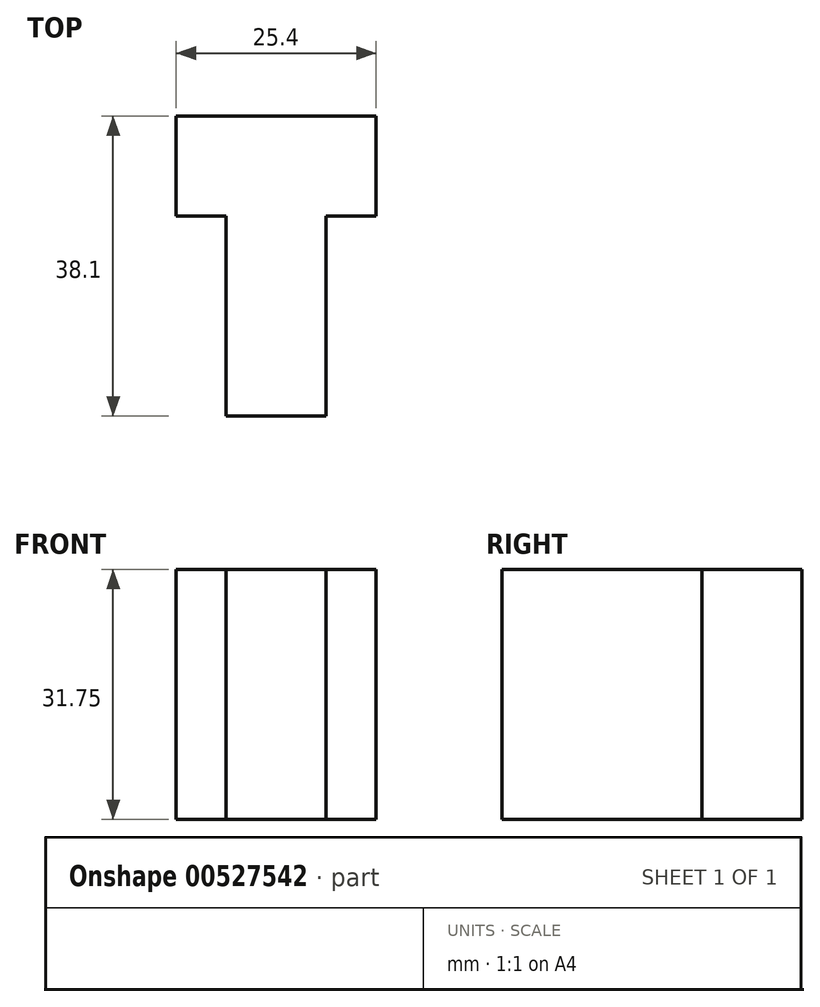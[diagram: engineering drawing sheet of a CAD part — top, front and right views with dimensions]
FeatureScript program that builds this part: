
annotation { "Feature Type Name" : "Feature", "Feature Type Description" : "" }
export const myFeature = defineFeature(function(context is Context, id is Id, definition is map)
    precondition{}
    {
        {
            var Q0;
            Q0=qCreatedBy(makeId("Top.planeOp"),FACE);
            var sketch = newSketch(context, id + "F0", { "sketchPlane" : qUnion([Q0])});
            skLineSegment(sketch, "E0", {"start": v(0, 0) * mm, "end": v(0, 25.4) * mm});
            skLineSegment(sketch, "E1", {"start": v(0, 25.4) * mm, "end": v(-6.35, 25.4) * mm});
            skLineSegment(sketch, "E2", {"start": v(-6.35, 25.4) * mm, "end": v(-6.35, 38.1) * mm});
            skLineSegment(sketch, "E3", {"start": v(-6.35, 38.1) * mm, "end": v(19.05, 38.1) * mm});
            skLineSegment(sketch, "E4", {"start": v(19.05, 38.1) * mm, "end": v(19.05, 25.4) * mm});
            skLineSegment(sketch, "E5", {"start": v(0, 0) * mm, "end": v(12.7, 0) * mm});
            skLineSegment(sketch, "E6", {"start": v(12.7, 0) * mm, "end": v(12.7, 25.4) * mm});
            skLineSegment(sketch, "E7", {"start": v(12.7, 25.4) * mm, "end": v(19.05, 25.4) * mm});
            skSolve(sketch);
        }
        {
            var Q0;
            Q0=makeQuery(id+"F0.imprint","IMPRINT",FACE,{"disambiguationData":[TD([[makeQuery(id+"F0.imprint","IMPRINT",EDGE,{"derivedFrom":sQuery(id+"F0.wireOp",EDGE,"E0")}),-1.0]])]});
            extrude(context, id + "F1", {"entities" : qUnion([Q0]), "depth" : 31.75 * mm, "offsetDistance" : 25.4 * mm});
        }
    });
